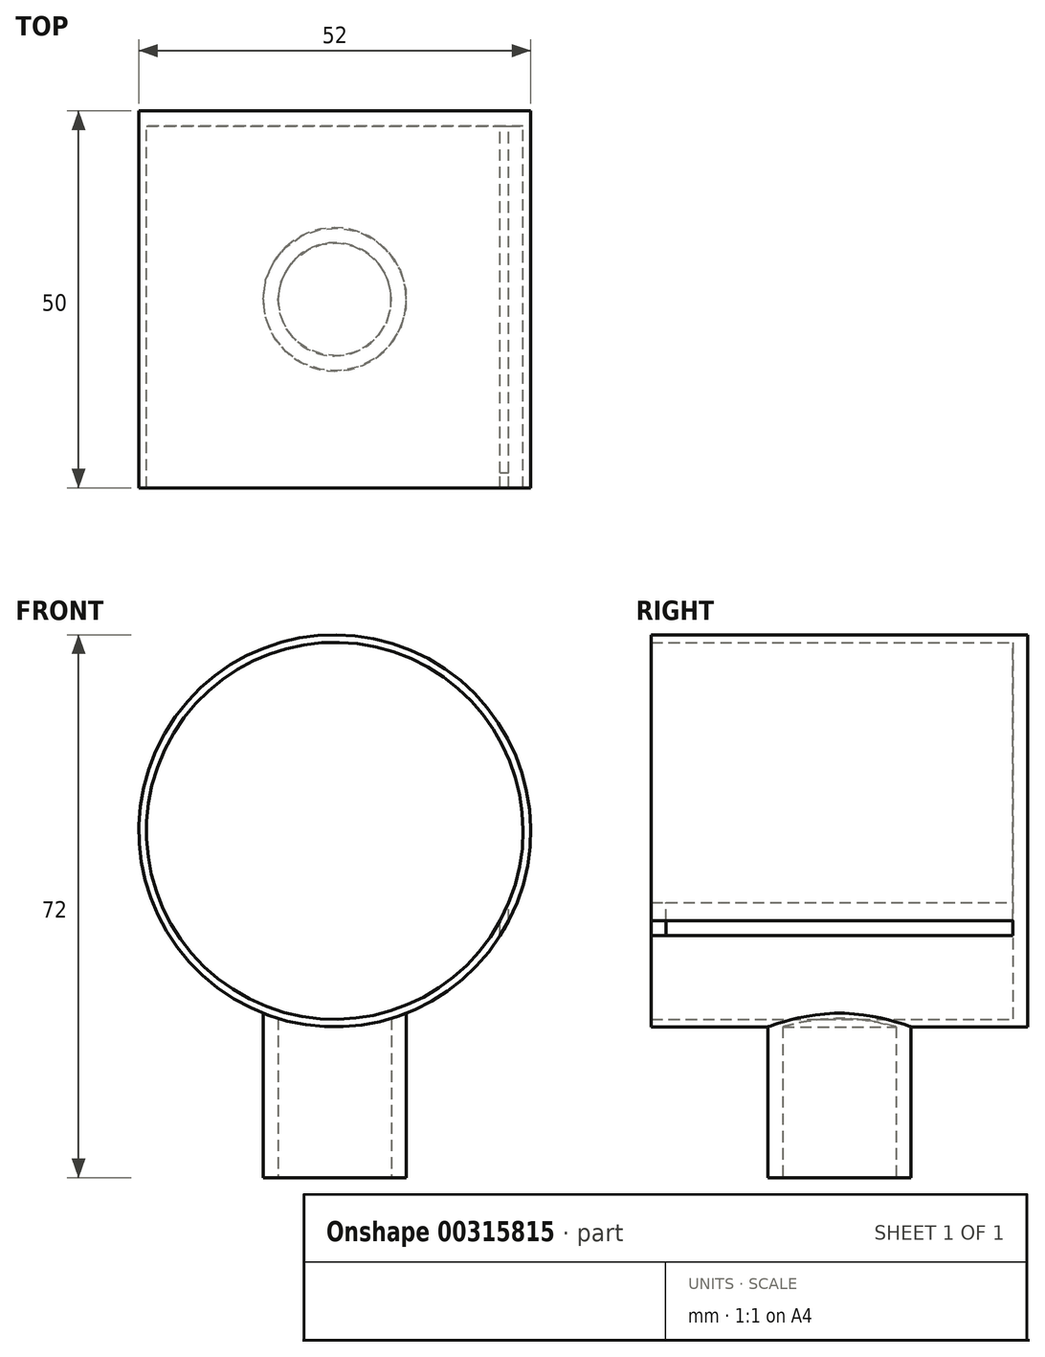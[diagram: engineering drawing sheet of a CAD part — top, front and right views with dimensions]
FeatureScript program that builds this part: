
annotation { "Feature Type Name" : "Feature", "Feature Type Description" : "" }
export const myFeature = defineFeature(function(context is Context, id is Id, definition is map)
    precondition{}
    {
        {
            var Q0;
            Q0=qCreatedBy(makeId("Front.planeOp"),FACE);
            var sketch = newSketch(context, id + "F0", { "sketchPlane" : qUnion([Q0])});
            skCircle(sketch, "E0", {"center": v(0, 26) * mm, "radius": 26 * mm});
            skCircle(sketch, "E1", {"center": v(0, 26) * mm, "radius": 25 * mm});
            skLineSegment(sketch, "E2", {"start": v(0, 26) * mm, "end": v(23.11, 14.1) * mm, "construction": true});
            skLineSegment(sketch, "E3", {"start": v(0, 26) * mm, "end": v(21.97, 12.1) * mm, "construction": true});
            skLineSegment(sketch, "E4", {"start": v(21.97, 12.1) * mm, "end": v(21.97, 14.07) * mm});
            skLineSegment(sketch, "E5", {"start": v(23.11, 14.1) * mm, "end": v(23.11, 16.48) * mm});
            skSolve(sketch);
        }
        {
            var Q0;
            {var subQ0=sQuery(id+"F0.wireOp",EDGE,"E1");var subQ1=makeQuery(id+"F0.imprint","INTERSECT",VERTEX,{"derivedFrom":[subQ0,sQuery(id+"F0.wireOp",EDGE,"SZOk9PFz-5vip-q86e-a5zU-gMkwcBEuY3OJ")]});Q0=makeQuery(id+"F0.imprint","IMPRINT",FACE,{"disambiguationData":[TD([[makeQuery(id+"F0.imprint","IMPRINT",EDGE,{"disambiguationData":[TD([[subQ1,-1.0]])],"derivedFrom":subQ0}),1.0]])]});}
            var Q1;
            {var subQ0=sQuery(id+"F0.wireOp",EDGE,"SZOk9PFz-5vip-q86e-a5zU-gMkwcBEuY3OJ");Q1=makeQuery(id+"F0.imprint","IMPRINT",FACE,{"disambiguationData":[TD([[makeQuery(id+"F0.imprint","IMPRINT",EDGE,{"derivedFrom":subQ0}),1.0]])]});}
            var Q2;
            {var subQ0=sQuery(id+"F0.wireOp",EDGE,"5oMtXElr-VzcF-lRva-Z6tl-CrBwbfyDiUFq");Q2=makeQuery(id+"F0.imprint","IMPRINT",FACE,{"disambiguationData":[TD([[makeQuery(id+"F0.imprint","IMPRINT",EDGE,{"derivedFrom":subQ0}),-1.0]])]});}
            var Q3;
            {var subQ0=sQuery(id+"F0.wireOp",EDGE,"E4");Q3=makeQuery(id+"F0.imprint","IMPRINT",FACE,{"disambiguationData":[TD([[makeQuery(id+"F0.imprint","IMPRINT",EDGE,{"derivedFrom":subQ0}),-1.0]])]});}
            extrude(context, id + "F1", {"entities" : qUnion([Q0, Q1, Q2, Q3]), "depth" : 2 * mm});
        }
        {
            var Q0;
            {var subQ0=sQuery(id+"F0.wireOp",EDGE,"SZOk9PFz-5vip-q86e-a5zU-gMkwcBEuY3OJ");Q0=makeQuery(id+"F0.imprint","IMPRINT",FACE,{"disambiguationData":[TD([[makeQuery(id+"F0.imprint","IMPRINT",EDGE,{"derivedFrom":subQ0}),-1.0]])]});}
            var Q1;
            {var subQ0=sQuery(id+"F0.wireOp",EDGE,"5oMtXElr-VzcF-lRva-Z6tl-CrBwbfyDiUFq");Q1=makeQuery(id+"F0.imprint","IMPRINT",FACE,{"disambiguationData":[TD([[makeQuery(id+"F0.imprint","IMPRINT",EDGE,{"derivedFrom":subQ0}),1.0]])]});}
            var Q2;
            {var subQ0=sQuery(id+"F0.wireOp",EDGE,"E4");Q2=makeQuery(id+"F0.imprint","IMPRINT",FACE,{"disambiguationData":[TD([[makeQuery(id+"F0.imprint","IMPRINT",EDGE,{"derivedFrom":subQ0}),1.0]])]});}
            extrude(context, id + "F2", {"entities" : qUnion([Q0, Q1, Q2]), "operationType" : NewBodyOperationType.ADD, "depth" : 50 * mm});
        }
        {
            var Q0;
            Q0=qCreatedBy(makeId("Top.planeOp"),FACE);
            var sketch = newSketch(context, id + "F3", { "sketchPlane" : qUnion([Q0])});
            skLineSegment(sketch, "E6", {"start": v(0, -50) * mm, "end": v(0, 0) * mm, "construction": true});
            skCircle(sketch, "E7", {"center": v(0, -25) * mm, "radius": 7.5 * mm});
            skCircle(sketch, "E8", {"center": v(0, -25) * mm, "radius": 9.5 * mm});
            skSolve(sketch);
        }
        {
            var Q0;
            Q0=makeQuery(id+"F3.imprint","IMPRINT",FACE,{"disambiguationData":[TD([[makeQuery(id+"F3.imprint","IMPRINT",EDGE,{"derivedFrom":sQuery(id+"F3.wireOp",EDGE,"E7")}),-1.0]])]});
            extrude(context, id + "F4", {"entities" : qUnion([Q0]), "operationType" : NewBodyOperationType.ADD, "depth" : 5 * mm});
        }
        {
            var Q0;
            Q0=makeQuery(id+"F3.imprint","IMPRINT",FACE,{"disambiguationData":[TD([[makeQuery(id+"F3.imprint","IMPRINT",EDGE,{"derivedFrom":sQuery(id+"F3.wireOp",EDGE,"E7")}),-1.0]])]});
            extrude(context, id + "F5", {"entities" : qUnion([Q0]), "operationType" : NewBodyOperationType.ADD, "oppositeDirection" : true, "depth" : 20 * mm});
        }
        {
            var Q0;
            Q0=makeQuery(id+"F1.opExtrude","CAP_FACE",FACE,{"disambiguationData":[OSD([sQuery(id+"F0.wireOp",EDGE,"E0"),sQuery(id+"F0.wireOp",EDGE,"E1"),sQuery(id+"F0.wireOp",EDGE,"5oMtXElr-VzcF-lRva-Z6tl-CrBwbfyDiUFq"),sQuery(id+"F0.wireOp",EDGE,"DXFd8KqK-meq6-J6tV-IH2f-xsUbXPtxahYL")])],"isStart":false});
            extrude(context, id + "F6", {"entities" : qUnion([Q0]), "operationType" : NewBodyOperationType.REMOVE, "depth" : 60 * mm});
        }
        {
            var Q0;
            Q0=makeQuery(id+"F2.opExtrude","CAP_FACE",FACE,{"disambiguationData":[OSD([sQuery(id+"F0.wireOp",EDGE,"E0"),sQuery(id+"F0.wireOp",EDGE,"E1"),sQuery(id+"F0.wireOp",EDGE,"E4"),sQuery(id+"F0.wireOp",EDGE,"E5")])],"isStart":false});
            var sketch = newSketch(context, id + "F7", { "sketchPlane" : qUnion([Q0])});
            skLineSegment(sketch, "E9", {"start": v(21.97, 14.07) * mm, "end": v(23.11, 16.48) * mm});
            skLineSegment(sketch, "E10", {"start": v(21.97, 12.1) * mm, "end": v(23.11, 14.1) * mm});
            skSolve(sketch);
        }
        {
            var Q0;
            Q0=makeQuery(id+"F7.imprint","IMPRINT",FACE,{"disambiguationData":[TD([[makeQuery(id+"F7.imprint","IMPRINT",EDGE,{"derivedFrom":sQuery(id+"F7.wireOp",EDGE,"E9")}),-1.0]])]});
            extrude(context, id + "F8", {"entities" : qUnion([Q0]), "operationType" : NewBodyOperationType.ADD, "oppositeDirection" : true, "depth" : 2 * mm});
        }
    });
